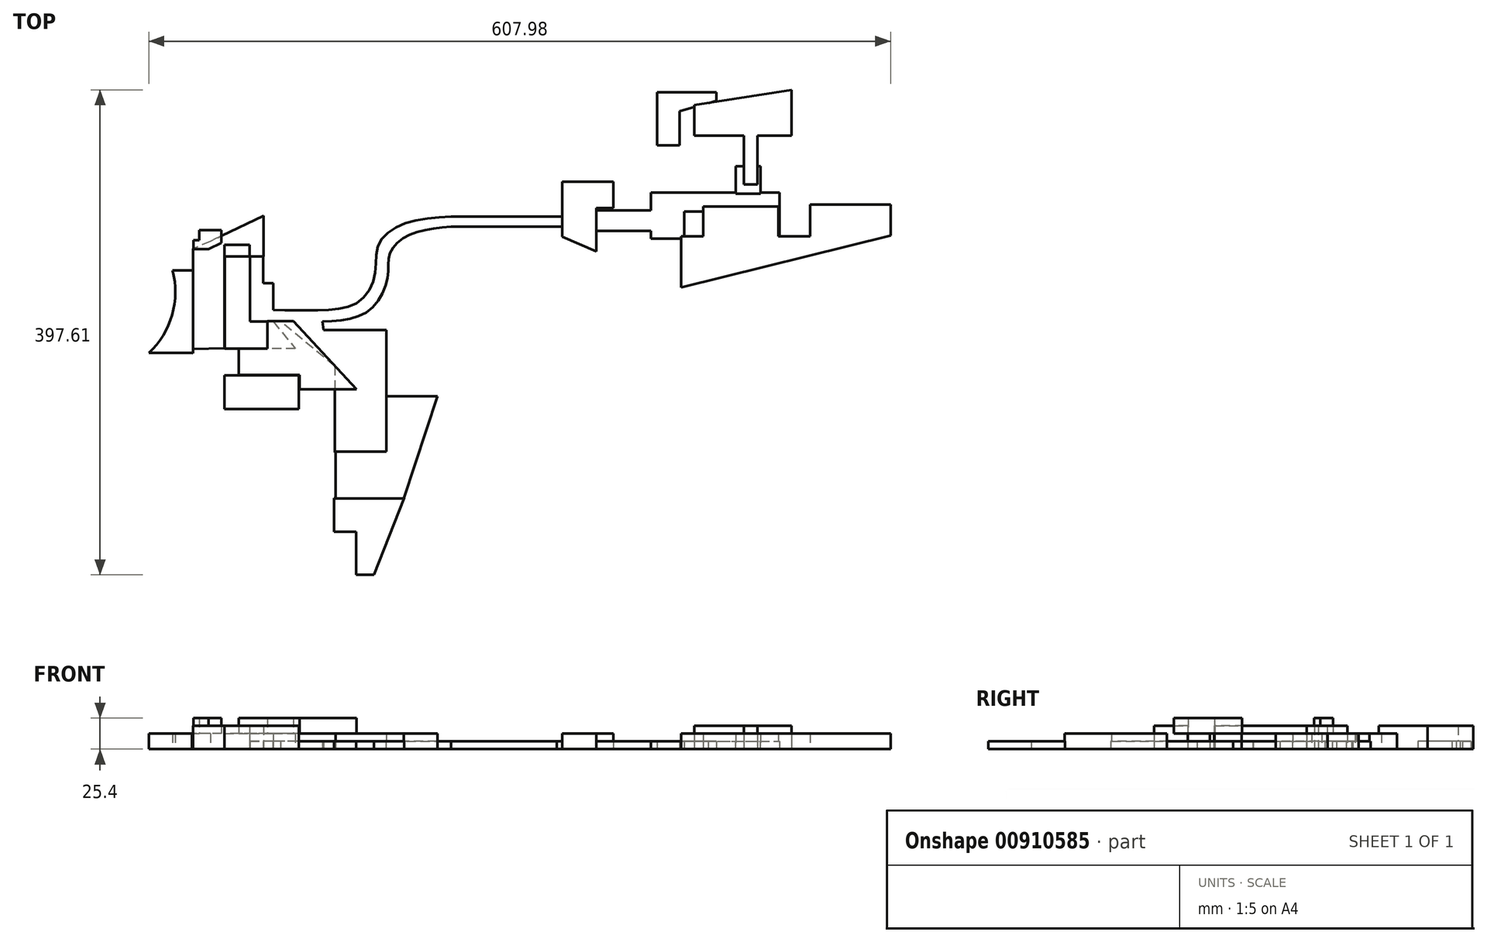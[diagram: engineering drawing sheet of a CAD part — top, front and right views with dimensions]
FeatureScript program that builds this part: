
annotation { "Feature Type Name" : "Feature", "Feature Type Description" : "" }
export const myFeature = defineFeature(function(context is Context, id is Id, definition is map)
    precondition{}
    {
        {
            var Q0;
            Q0=qCreatedBy(makeId("Top.planeOp"),FACE);
            var sketch = newSketch(context, id + "F0", { "sketchPlane" : qUnion([Q0])});
            skLineSegment(sketch, "E0.bottom", {"start": v(-96.63, 55.02) * mm, "end": v(8.67, 55.02) * mm});
            skLineSegment(sketch, "E0.left", {"start": v(-96.63, 55.02) * mm, "end": v(-96.63, 17.26) * mm});
            skLineSegment(sketch, "E0.right", {"start": v(8.67, 55.02) * mm, "end": v(8.67, 17.26) * mm});
            skLineSegment(sketch, "E1.top", {"start": v(-69.35, 39.22) * mm, "end": v(-14.4, 39.22) * mm});
            skLineSegment(sketch, "E1.right", {"start": v(-14.4, 17.26) * mm, "end": v(-14.4, 39.22) * mm});
            skLineSegment(sketch, "E2", {"start": v(-96.63, 17.26) * mm, "end": v(-69.35, 17.26) * mm});
            skLineSegment(sketch, "E3", {"start": v(-69.35, 39.22) * mm, "end": v(-69.35, 17.26) * mm});
            skLineSegment(sketch, "E4", {"start": v(-14.4, 17.26) * mm, "end": v(8.67, 17.26) * mm});
            skLineSegment(sketch, "E5", {"start": v(-96.63, 40.24) * mm, "end": v(-157.06, 40.24) * mm});
            skLineSegment(sketch, "E6", {"start": v(-157.06, 40.24) * mm, "end": v(-157.06, 23.32) * mm});
            skLineSegment(sketch, "E7", {"start": v(-157.06, 23.32) * mm, "end": v(-96.63, 23.32) * mm});
            skLineSegment(sketch, "E8.bottom", {"start": v(-173.85, 35.23) * mm, "end": v(-260.44, 35.23) * mm});
            skLineSegment(sketch, "E8.top", {"start": v(-173.85, 26.97) * mm, "end": v(-260.44, 26.97) * mm});
            skLineSegment(sketch, "E8.left", {"start": v(-173.85, 35.23) * mm, "end": v(-173.85, 26.97) * mm});
            skLineSegment(sketch, "E8.right", {"start": v(-260.44, 35.23) * mm, "end": v(-260.44, 26.97) * mm});
            skFitSpline(sketch, "E9", {"points": [v(-260.44, 35.23) * mm, v(-301.5, 28.35) * mm, v(-320.47, 10.91) * mm, v(-323.03, -13.44) * mm, v(-337.4, -35.4) * mm, v(-366.72, -41.43) * mm, v(-406.13, -41.47) * mm], "startDerivative": vector(-228.43, -16) * mm, "endDerivative": vector(-213.5, 2.55) * mm});
            skLineSegment(sketch, "E10", {"start": v(-406.13, -41.47) * mm, "end": v(-406.13, -50.74) * mm});
            skPoint(sketch, "E11.2.internal.snap0", {"position": v(-406.13, -46.1) * mm});
            skFitSpline(sketch, "E12", {"points": [v(-406.13, -50.74) * mm, v(-366.03, -50.74) * mm, v(-328.3, -42.23) * mm, v(-312.43, -14.16) * mm, v(-310.82, 4.7) * mm, v(-294.71, 20.11) * mm, v(-260.44, 26.97) * mm], "startDerivative": vector(206.76, -2.92) * mm, "endDerivative": vector(206.76, 19.84) * mm});
            skLineSegment(sketch, "E13", {"start": v(-406.13, -41.47) * mm, "end": v(-406.13, -19.45) * mm});
            skLineSegment(sketch, "E14", {"start": v(-406.13, -19.45) * mm, "end": v(-414.34, -19.45) * mm});
            skLineSegment(sketch, "E15", {"start": v(-414.34, -19.45) * mm, "end": v(-414.34, 2.4) * mm});
            skLineSegment(sketch, "E16", {"start": v(-406.13, -50.74) * mm, "end": v(-425.15, -50.74) * mm});
            skLineSegment(sketch, "E17", {"start": v(-425.15, -50.74) * mm, "end": v(-425.15, 2.4) * mm});
            skLineSegment(sketch, "E18", {"start": v(-425.15, 2.4) * mm, "end": v(-414.34, 2.4) * mm});
            skLineSegment(sketch, "E19.bottom", {"start": v(-173.85, 35.23) * mm, "end": v(-168.56, 35.23) * mm});
            skLineSegment(sketch, "E19.top", {"start": v(-173.85, 26.94) * mm, "end": v(-168.56, 26.94) * mm});
            skLineSegment(sketch, "E19.left", {"start": v(-173.85, 35.23) * mm, "end": v(-173.85, 26.94) * mm});
            skLineSegment(sketch, "E19.right", {"start": v(-168.56, 35.23) * mm, "end": v(-168.56, 26.94) * mm});
            skLineSegment(sketch, "E20", {"start": v(-42.96, 130.2) * mm, "end": v(-73.06, 121.54) * mm});
            skLineSegment(sketch, "E21", {"start": v(-42.96, 130.2) * mm, "end": v(-42.96, 137.13) * mm});
            skLineSegment(sketch, "E22", {"start": v(-42.96, 137.13) * mm, "end": v(-91.68, 137.13) * mm});
            skLineSegment(sketch, "E23", {"start": v(-73.06, 121.54) * mm, "end": v(-73.06, 93.6) * mm});
            skLineSegment(sketch, "E24", {"start": v(-91.68, 137.13) * mm, "end": v(-91.68, 93.6) * mm});
            skLineSegment(sketch, "E25", {"start": v(-91.68, 93.6) * mm, "end": v(-73.06, 93.6) * mm});
            skLineSegment(sketch, "E26", {"start": v(-355.89, -87.5) * mm, "end": v(-400.31, -50.82) * mm});
            skLineSegment(sketch, "E27", {"start": v(-355.89, -87.5) * mm, "end": v(-355.89, -103.85) * mm});
            skLineSegment(sketch, "E28", {"start": v(-355.89, -103.85) * mm, "end": v(-355.89, -158.25) * mm});
            skLineSegment(sketch, "E29", {"start": v(-355.89, -158.25) * mm, "end": v(-313.48, -158.25) * mm});
            skLineSegment(sketch, "E30", {"start": v(-313.48, -158.25) * mm, "end": v(-313.48, -57.96) * mm});
            skLineSegment(sketch, "E31", {"start": v(-313.48, -57.96) * mm, "end": v(-365.02, -57.96) * mm});
            skLineSegment(sketch, "E32", {"start": v(-365.02, -57.96) * mm, "end": v(-366.03, -50.74) * mm});
            skLineSegment(sketch, "E33", {"start": v(-334.83, -195.5) * mm, "end": v(-303.23, -195.5) * mm});
            skLineSegment(sketch, "E34", {"start": v(-334.83, -195.5) * mm, "end": v(-356.27, -195.5) * mm});
            skLineSegment(sketch, "E35", {"start": v(-356.27, -195.5) * mm, "end": v(-356.27, -223.34) * mm});
            skLineSegment(sketch, "E36", {"start": v(-303.23, -195.5) * mm, "end": v(-298.9, -195.5) * mm});
            skLineSegment(sketch, "E37", {"start": v(-323.71, -258.58) * mm, "end": v(-298.9, -195.5) * mm});
            skLineSegment(sketch, "E38", {"start": v(-356.27, -223.34) * mm, "end": v(-338.27, -223.34) * mm});
            skLineSegment(sketch, "E39", {"start": v(-338.27, -258.58) * mm, "end": v(-323.71, -258.58) * mm});
            skLineSegment(sketch, "E40", {"start": v(-338.27, -258.58) * mm, "end": v(-338.27, -223.34) * mm});
            skSolve(sketch);
        }
        {
            var Q0;
            {var subQ0=sQuery(id+"F0.wireOp",EDGE,"E5");Q0=makeQuery(id+"F0.imprint","IMPRINT",FACE,{"disambiguationData":[TD([[makeQuery(id+"F0.imprint","IMPRINT",EDGE,{"derivedFrom":subQ0}),1.0]])]});}
            var Q1;
            {var subQ4=sQuery(id+"F0.wireOp",EDGE,"E0.bottom");Q1=makeQuery(id+"F0.imprint","IMPRINT",FACE,{"disambiguationData":[TD([[makeQuery(id+"F0.imprint","IMPRINT",EDGE,{"derivedFrom":subQ4}),-1.0]])]});}
            var Q2;
            Q2=makeQuery(id+"F0.imprint","IMPRINT",FACE,{"disambiguationData":[TD([[makeQuery(id+"F0.imprint","IMPRINT",EDGE,{"derivedFrom":sQuery(id+"F0.wireOp",EDGE,"E8.right")}),-1.0]])]});
            var Q3;
            Q3=makeQuery(id+"F0.imprint","IMPRINT",FACE,{"disambiguationData":[TD([[makeQuery(id+"F0.imprint","IMPRINT",EDGE,{"derivedFrom":sQuery(id+"F0.wireOp",EDGE,"E10")}),-1.0]])]});
            var Q4;
            Q4=makeQuery(id+"F0.imprint","IMPRINT",FACE,{"disambiguationData":[TD([[makeQuery(id+"F0.imprint","IMPRINT",EDGE,{"derivedFrom":sQuery(id+"F0.wireOp",EDGE,"E8.bottom")}),1.0]])]});
            var Q5;
            {var subQ3=sQuery(id+"F0.wireOp",EDGE,"E19.bottom");Q5=makeQuery(id+"F0.imprint","IMPRINT",FACE,{"disambiguationData":[TD([[makeQuery(id+"F0.imprint","IMPRINT",EDGE,{"derivedFrom":subQ3}),-1.0]])]});}
            var Q6;
            Q6=makeQuery(id+"F0.imprint","IMPRINT",FACE,{"disambiguationData":[TD([[makeQuery(id+"F0.imprint","IMPRINT",EDGE,{"derivedFrom":sQuery(id+"F0.wireOp",EDGE,"E20")}),-1.0]])]});
            var Q7;
            {var subQ0=sQuery(id+"F0.wireOp",EDGE,"E26");Q7=makeQuery(id+"F0.imprint","IMPRINT",FACE,{"disambiguationData":[TD([[makeQuery(id+"F0.imprint","IMPRINT",EDGE,{"derivedFrom":subQ0}),-1.0]])]});}
            var Q8;
            Q8=makeQuery(id+"F0.imprint","IMPRINT",FACE,{"disambiguationData":[TD([[makeQuery(id+"F0.imprint","IMPRINT",EDGE,{"derivedFrom":sQuery(id+"F0.wireOp",EDGE,"E33")}),-1.0]])]});
            extrude(context, id + "F1", {"entities" : qUnion([Q0, Q1, Q2, Q3, Q4, Q5, Q6, Q7, Q8]), "depth" : 6.35 * mm, "offsetDistance" : 25.4 * mm});
        }
        {
            var Q0;
            Q0=qCreatedBy(makeId("Top.planeOp"),FACE);
            var sketch = newSketch(context, id + "F2", { "sketchPlane" : qUnion([Q0])});
            skLineSegment(sketch, "E41", {"start": v(-71.8, 19.1) * mm, "end": v(-71.8, -23) * mm});
            skLineSegment(sketch, "E42", {"start": v(-71.8, -23) * mm, "end": v(99.8, 19.6) * mm});
            skLineSegment(sketch, "E43", {"start": v(99.8, 19.6) * mm, "end": v(99.8, 45) * mm});
            skLineSegment(sketch, "E44", {"start": v(99.8, 45) * mm, "end": v(33.96, 45) * mm});
            skLineSegment(sketch, "E45", {"start": v(33.96, 45) * mm, "end": v(33.96, 19.07) * mm});
            skLineSegment(sketch, "E46", {"start": v(33.96, 19.07) * mm, "end": v(7.89, 19.07) * mm});
            skLineSegment(sketch, "E47", {"start": v(7.89, 19.07) * mm, "end": v(7.89, 43.57) * mm});
            skLineSegment(sketch, "E48", {"start": v(7.89, 43.57) * mm, "end": v(-53.68, 43.57) * mm});
            skLineSegment(sketch, "E49", {"start": v(-53.68, 43.57) * mm, "end": v(-53.68, 19.11) * mm});
            skLineSegment(sketch, "E50", {"start": v(-53.68, 19.11) * mm, "end": v(-71.8, 19.1) * mm});
            skLineSegment(sketch, "E51", {"start": v(-169.4, 63.74) * mm, "end": v(-169.4, 30.07) * mm});
            skLineSegment(sketch, "E52", {"start": v(-169.4, 63.74) * mm, "end": v(-127.39, 63.74) * mm});
            skLineSegment(sketch, "E53", {"start": v(-127.39, 63.74) * mm, "end": v(-127.39, 42.16) * mm});
            skLineSegment(sketch, "E54", {"start": v(-127.39, 42.16) * mm, "end": v(-141.5, 42.16) * mm});
            skLineSegment(sketch, "E55", {"start": v(-169.4, 18.56) * mm, "end": v(-169.4, 30.07) * mm});
            skLineSegment(sketch, "E56", {"start": v(-141.5, 42.16) * mm, "end": v(-141.5, 6.67) * mm});
            skLineSegment(sketch, "E57", {"start": v(-169.4, 18.56) * mm, "end": v(-141.5, 6.67) * mm});
            skLineSegment(sketch, "E58.left", {"start": v(-425.19, 2.53) * mm, "end": v(-425.19, -50.95) * mm});
            skLineSegment(sketch, "E59", {"start": v(-425.19, -50.95) * mm, "end": v(-406.27, -50.95) * mm});
            skLineSegment(sketch, "E60", {"start": v(-406.27, -50.95) * mm, "end": v(-388.22, -72.94) * mm});
            skLineSegment(sketch, "E61", {"start": v(-388.22, -72.94) * mm, "end": v(-446.04, -72.94) * mm});
            skLineSegment(sketch, "E62", {"start": v(-446.04, -72.94) * mm, "end": v(-446.04, 2.53) * mm});
            skLineSegment(sketch, "E63", {"start": v(-446.04, 2.53) * mm, "end": v(-425.19, 2.53) * mm});
            skLineSegment(sketch, "E64.bottom", {"start": v(-6.88, 54.06) * mm, "end": v(-27.27, 54.06) * mm});
            skLineSegment(sketch, "E64.top", {"start": v(-6.88, 76.46) * mm, "end": v(-27.27, 76.46) * mm});
            skLineSegment(sketch, "E64.left", {"start": v(-6.88, 54.06) * mm, "end": v(-6.88, 76.46) * mm});
            skLineSegment(sketch, "E64.right", {"start": v(-27.27, 54.06) * mm, "end": v(-27.27, 76.46) * mm});
            skLineSegment(sketch, "E65", {"start": v(-313.49, -157.38) * mm, "end": v(-313.49, -111.97) * mm});
            skLineSegment(sketch, "E66", {"start": v(-313.49, -111.97) * mm, "end": v(-271.5, -111.97) * mm});
            skLineSegment(sketch, "E67", {"start": v(-271.5, -111.97) * mm, "end": v(-300.2, -198.51) * mm});
            skLineSegment(sketch, "E68", {"start": v(-313.49, -157.38) * mm, "end": v(-355.18, -157.38) * mm});
            skLineSegment(sketch, "E69", {"start": v(-355.18, -157.38) * mm, "end": v(-355.18, -195.99) * mm});
            skLineSegment(sketch, "E70", {"start": v(-355.18, -195.99) * mm, "end": v(-299.37, -195.99) * mm});
            skLineSegment(sketch, "E71", {"start": v(-271.5, -111.97) * mm, "end": v(-321.65, -263.17) * mm});
            skLineSegment(sketch, "E72", {"start": v(-472.99, -8.83) * mm, "end": v(-488.76, -8.83) * mm});
            skArc(sketch, "E73", {"start": v(-508.19, -76.7) * mm, "mid": v(-489.15, -45.43) * mm, "end": v(-488.76, -8.83) * mm});
            skLineSegment(sketch, "E74", {"start": v(-508.19, -76.7) * mm, "end": v(-474.84, -76.7) * mm});
            skLineSegment(sketch, "E75", {"start": v(-474.84, -76.7) * mm, "end": v(-473, -76.7) * mm});
            skLineSegment(sketch, "E76", {"start": v(-472.07, -69.53) * mm, "end": v(-472.07, -76.76) * mm});
            skLineSegment(sketch, "E77", {"start": v(-472.07, -76.76) * mm, "end": v(-473, -76.7) * mm});
            skLineSegment(sketch, "E78", {"start": v(-472.07, -69.53) * mm, "end": v(-472.07, -59.95) * mm});
            skLineSegment(sketch, "E79", {"start": v(-472.07, -59.95) * mm, "end": v(-472.07, -8.82) * mm});
            skLineSegment(sketch, "E80", {"start": v(-472.07, -8.82) * mm, "end": v(-472.99, -8.83) * mm});
            skSolve(sketch);
        }
        {
            var Q0;
            Q0=makeQuery(id+"F2.imprint","IMPRINT",FACE,{"disambiguationData":[TD([[makeQuery(id+"F2.imprint","IMPRINT",EDGE,{"derivedFrom":sQuery(id+"F2.wireOp",EDGE,"E41")}),1.0]])]});
            var Q1;
            Q1=makeQuery(id+"F2.imprint","IMPRINT",FACE,{"disambiguationData":[TD([[makeQuery(id+"F2.imprint","IMPRINT",EDGE,{"derivedFrom":sQuery(id+"F2.wireOp",EDGE,"E51")}),1.0]])]});
            var Q2;
            Q2=makeQuery(id+"F2.imprint","IMPRINT",FACE,{"disambiguationData":[TD([[makeQuery(id+"F2.imprint","IMPRINT",EDGE,{"derivedFrom":sQuery(id+"F2.wireOp",EDGE,"E58.left")}),-1.0]])]});
            var Q3;
            Q3=makeQuery(id+"F2.imprint","IMPRINT",FACE,{"disambiguationData":[TD([[makeQuery(id+"F2.imprint","IMPRINT",EDGE,{"derivedFrom":sQuery(id+"F2.wireOp",EDGE,"E64.bottom")}),-1.0]])]});
            var Q4;
            Q4=makeQuery(id+"F2.imprint","IMPRINT",FACE,{"disambiguationData":[TD([[makeQuery(id+"F2.imprint","IMPRINT",EDGE,{"derivedFrom":sQuery(id+"F2.wireOp",EDGE,"E65")}),-1.0]])]});
            var Q5;
            Q5=makeQuery(id+"F2.imprint","IMPRINT",FACE,{"disambiguationData":[TD([[makeQuery(id+"F2.imprint","IMPRINT",EDGE,{"derivedFrom":sQuery(id+"F2.wireOp",EDGE,"WrapXvIz-eKti-euEe-2G05-Czecql6LrKci")}),-1.0]])]});
            var Q6;
            Q6=makeQuery(id+"F2.imprint","IMPRINT",FACE,{"disambiguationData":[TD([[makeQuery(id+"F2.imprint","IMPRINT",EDGE,{"derivedFrom":sQuery(id+"F2.wireOp",EDGE,"E72")}),1.0]])]});
            extrude(context, id + "F3", {"entities" : qUnion([Q0, Q1, Q2, Q3, Q4, Q5, Q6]), "operationType" : NewBodyOperationType.ADD, "depth" : 12.7 * mm, "offsetDistance" : 25.4 * mm});
        }
        {
            var Q0;
            Q0=qCreatedBy(makeId("Top.planeOp"),FACE);
            var sketch = newSketch(context, id + "F4", { "sketchPlane" : qUnion([Q0])});
            skLineSegment(sketch, "E81.bottom", {"start": v(-20.53, 61.5) * mm, "end": v(-9.39, 61.5) * mm});
            skLineSegment(sketch, "E81.top", {"start": v(-20.53, 101.58) * mm, "end": v(-9.39, 101.58) * mm});
            skLineSegment(sketch, "E81.left", {"start": v(-20.53, 61.5) * mm, "end": v(-20.53, 101.58) * mm});
            skLineSegment(sketch, "E81.right", {"start": v(-9.39, 61.5) * mm, "end": v(-9.39, 101.58) * mm});
            skLineSegment(sketch, "E82", {"start": v(-20.53, 101.58) * mm, "end": v(-60.96, 101.58) * mm});
            skLineSegment(sketch, "E83", {"start": v(-60.96, 101.58) * mm, "end": v(-60.96, 126.55) * mm});
            skLineSegment(sketch, "E84", {"start": v(-60.96, 126.55) * mm, "end": v(18.6, 139.03) * mm});
            skLineSegment(sketch, "E85", {"start": v(18.6, 139.03) * mm, "end": v(18.6, 101.58) * mm});
            skLineSegment(sketch, "E86", {"start": v(18.6, 101.58) * mm, "end": v(-9.39, 101.58) * mm});
            skLineSegment(sketch, "E87", {"start": v(-446.33, -72.7) * mm, "end": v(-446.33, 5.14) * mm});
            skLineSegment(sketch, "E88", {"start": v(-446.33, 5.14) * mm, "end": v(-446.33, 12.15) * mm});
            skLineSegment(sketch, "E89", {"start": v(-446.33, 12.15) * mm, "end": v(-425.62, 12.15) * mm});
            skLineSegment(sketch, "E90", {"start": v(-425.62, 12.15) * mm, "end": v(-425.62, 2.5) * mm});
            skLineSegment(sketch, "E91", {"start": v(-425.62, 2.5) * mm, "end": v(-414.22, 2.5) * mm});
            skLineSegment(sketch, "E92", {"start": v(-414.22, 2.5) * mm, "end": v(-414.22, 35.68) * mm});
            skLineSegment(sketch, "E93", {"start": v(-414.22, 35.68) * mm, "end": v(-457.63, 14.93) * mm});
            skLineSegment(sketch, "E94", {"start": v(-457.63, 14.93) * mm, "end": v(-472.1, 8.8) * mm});
            skLineSegment(sketch, "E95", {"start": v(-472.1, 8.8) * mm, "end": v(-472.1, -36.22) * mm});
            skLineSegment(sketch, "E96", {"start": v(-472.1, -36.22) * mm, "end": v(-472.1, -73.32) * mm});
            skLineSegment(sketch, "E97", {"start": v(-472.1, -73.32) * mm, "end": v(-446.33, -72.7) * mm});
            skLineSegment(sketch, "E98", {"start": v(-445.12, -122.57) * mm, "end": v(-385.18, -122.57) * mm});
            skLineSegment(sketch, "E99", {"start": v(-385.18, -122.57) * mm, "end": v(-385.18, -95.07) * mm});
            skLineSegment(sketch, "E100", {"start": v(-385.18, -95.07) * mm, "end": v(-446.33, -95.07) * mm});
            skLineSegment(sketch, "E101", {"start": v(-446.33, -95.07) * mm, "end": v(-446.33, -122.57) * mm});
            skLineSegment(sketch, "E102", {"start": v(-446.33, -122.57) * mm, "end": v(-445.12, -122.57) * mm});
            skLineSegment(sketch, "E103.bottom", {"start": v(-385.18, -122.57) * mm, "end": v(-414.75, -122.57) * mm});
            skLineSegment(sketch, "E103.top", {"start": v(-385.18, -194.7) * mm, "end": v(-414.75, -194.7) * mm});
            skLineSegment(sketch, "E103.left", {"start": v(-385.18, -122.57) * mm, "end": v(-385.18, -194.7) * mm});
            skLineSegment(sketch, "E103.right", {"start": v(-414.75, -122.57) * mm, "end": v(-414.75, -194.7) * mm});
            skSolve(sketch);
        }
        {
            var Q0;
            Q0=makeQuery(id+"F4.imprint","IMPRINT",FACE,{"disambiguationData":[TD([[makeQuery(id+"F4.imprint","IMPRINT",EDGE,{"derivedFrom":sQuery(id+"F4.wireOp",EDGE,"E81.top")}),1.0]])]});
            var Q1;
            Q1=makeQuery(id+"F4.imprint","IMPRINT",FACE,{"disambiguationData":[TD([[makeQuery(id+"F4.imprint","IMPRINT",EDGE,{"derivedFrom":sQuery(id+"F4.wireOp",EDGE,"E81.bottom")}),1.0]])]});
            var Q2;
            Q2=makeQuery(id+"F4.imprint","IMPRINT",FACE,{"disambiguationData":[TD([[makeQuery(id+"F4.imprint","IMPRINT",EDGE,{"derivedFrom":sQuery(id+"F4.wireOp",EDGE,"E87")}),1.0]])]});
            var Q3;
            Q3=makeQuery(id+"F4.imprint","IMPRINT",FACE,{"disambiguationData":[TD([[makeQuery(id+"F4.imprint","IMPRINT",EDGE,{"derivedFrom":sQuery(id+"F4.wireOp",EDGE,"E98")}),1.0]])]});
            var Q4;
            Q4=makeQuery(id+"F4.imprint","IMPRINT",FACE,{"disambiguationData":[TD([[makeQuery(id+"F4.imprint","IMPRINT",EDGE,{"derivedFrom":sQuery(id+"F4.wireOp",EDGE,"E103.bottom")}),1.0]])]});
            extrude(context, id + "F5", {"entities" : qUnion([Q0, Q1, Q2, Q3, Q4]), "operationType" : NewBodyOperationType.ADD, "depth" : 19.05 * mm, "offsetDistance" : 25.4 * mm});
        }
        {
            var Q0;
            Q0=qCreatedBy(makeId("Top.planeOp"),FACE);
            var sketch = newSketch(context, id + "F6", { "sketchPlane" : qUnion([Q0])});
            skLineSegment(sketch, "E104.bottom", {"start": v(-434.44, -73.16) * mm, "end": v(-415.23, -73.16) * mm});
            skLineSegment(sketch, "E104.top", {"start": v(-434.44, -94.78) * mm, "end": v(-415.23, -94.78) * mm});
            skLineSegment(sketch, "E104.left", {"start": v(-434.44, -73.16) * mm, "end": v(-434.44, -94.78) * mm});
            skLineSegment(sketch, "E104.right", {"start": v(-415.23, -73.16) * mm, "end": v(-415.23, -94.78) * mm});
            skLineSegment(sketch, "E105", {"start": v(-410.96, -50.48) * mm, "end": v(-410.96, -73.16) * mm});
            skLineSegment(sketch, "E106", {"start": v(-410.96, -73.16) * mm, "end": v(-415.23, -73.16) * mm});
            skLineSegment(sketch, "E107", {"start": v(-384.8, -94.78) * mm, "end": v(-415.23, -94.78) * mm});
            skLineSegment(sketch, "E108", {"start": v(-384.8, -94.78) * mm, "end": v(-384.8, -106.25) * mm});
            skLineSegment(sketch, "E109", {"start": v(-384.8, -106.25) * mm, "end": v(-338.1, -106.25) * mm});
            skLineSegment(sketch, "E110", {"start": v(-338.1, -106.25) * mm, "end": v(-389.87, -50.48) * mm});
            skLineSegment(sketch, "E111", {"start": v(-389.87, -50.48) * mm, "end": v(-410.96, -50.48) * mm});
            skLineSegment(sketch, "E112", {"start": v(-471.76, 8.64) * mm, "end": v(-459.2, 8.64) * mm});
            skLineSegment(sketch, "E113", {"start": v(-459.2, 8.64) * mm, "end": v(-448.64, 13.7) * mm});
            skLineSegment(sketch, "E114", {"start": v(-448.64, 13.7) * mm, "end": v(-448.64, 24.01) * mm});
            skLineSegment(sketch, "E115", {"start": v(-448.64, 24.01) * mm, "end": v(-466.93, 24.01) * mm});
            skLineSegment(sketch, "E116", {"start": v(-466.93, 24.01) * mm, "end": v(-466.93, 15.82) * mm});
            skLineSegment(sketch, "E117", {"start": v(-471.76, 8.64) * mm, "end": v(-471.76, 15.82) * mm});
            skLineSegment(sketch, "E118", {"start": v(-471.76, 15.82) * mm, "end": v(-466.93, 15.82) * mm});
            skSolve(sketch);
        }
        {
            var Q0;
            Q0=makeQuery(id+"F6.imprint","IMPRINT",FACE,{"disambiguationData":[TD([[makeQuery(id+"F6.imprint","IMPRINT",EDGE,{"derivedFrom":sQuery(id+"F6.wireOp",EDGE,"E104.right")}),1.0]])]});
            var Q1;
            Q1=makeQuery(id+"F6.imprint","IMPRINT",FACE,{"disambiguationData":[TD([[makeQuery(id+"F6.imprint","IMPRINT",EDGE,{"derivedFrom":sQuery(id+"F6.wireOp",EDGE,"E104.bottom")}),-1.0]])]});
            var Q2;
            Q2=makeQuery(id+"F6.imprint","IMPRINT",FACE,{"disambiguationData":[TD([[makeQuery(id+"F6.imprint","IMPRINT",EDGE,{"derivedFrom":sQuery(id+"F6.wireOp",EDGE,"E112")}),1.0]])]});
            extrude(context, id + "F7", {"entities" : qUnion([Q0, Q1, Q2]), "operationType" : NewBodyOperationType.ADD, "depth" : 25.4 * mm, "offsetDistance" : 25.4 * mm, "hasSecondDirection" : true, "secondDirectionOppositeDirection" : false, "secondDirectionDepth" : 12.7 * mm});
        }
    });
